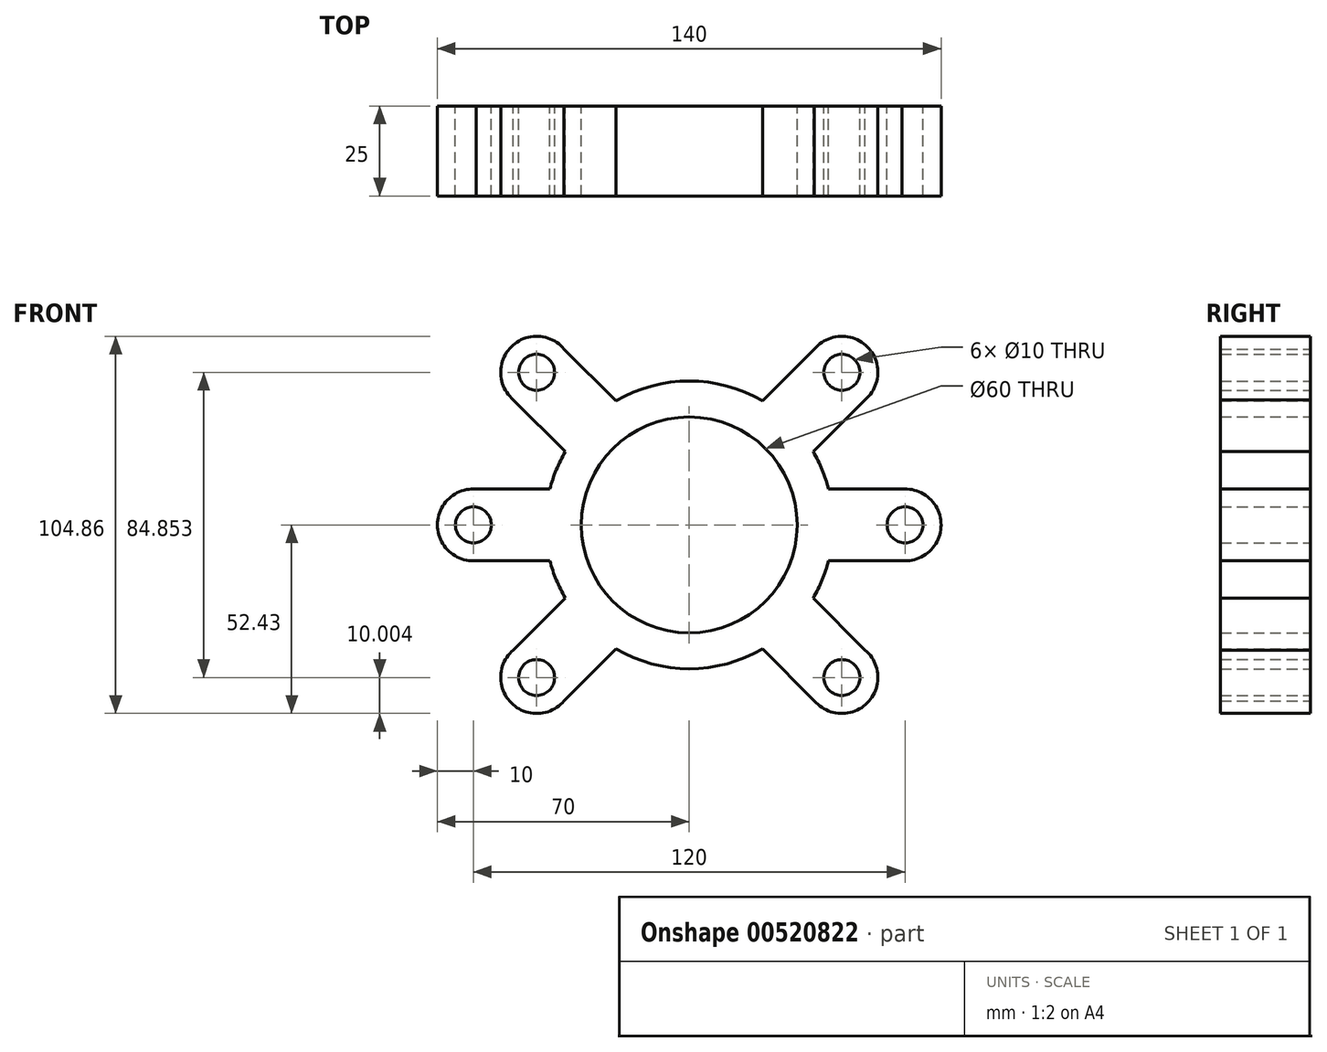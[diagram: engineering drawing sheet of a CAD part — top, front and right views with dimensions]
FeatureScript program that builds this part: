
annotation { "Feature Type Name" : "Feature", "Feature Type Description" : "" }
export const myFeature = defineFeature(function(context is Context, id is Id, definition is map)
    precondition{}
    {
        {
            var Q0;
            Q0=qCreatedBy(makeId("Front.planeOp"),FACE);
            var sketch = newSketch(context, id + "F0", { "sketchPlane" : qUnion([Q0])});
            skCircle(sketch, "E0", {"center": v(0, 0) * mm, "radius": 60 * mm, "construction": true});
            skCircle(sketch, "E1", {"center": v(0, 0) * mm, "radius": 30 * mm});
            skArc(sketch, "E2", {"start": v(38.74, 9.97) * mm, "mid": v(36.96, 15.3) * mm, "end": v(34.44, 20.35) * mm});
            skArc(sketch, "E3", {"start": v(59.17, -9.97) * mm, "mid": v(70, 0) * mm, "end": v(59.17, 9.97) * mm});
            skCircle(sketch, "E4", {"center": v(60, 0) * mm, "radius": 5 * mm});
            skLineSegment(sketch, "E5", {"start": v(59.17, 9.97) * mm, "end": v(38.74, 9.97) * mm});
            skLineSegment(sketch, "E6", {"start": v(59.17, -9.97) * mm, "end": v(38.74, -9.97) * mm});
            skLineSegment(sketch, "E7.1.0", {"start": v(34.8, 48.88) * mm, "end": v(20.35, 34.44) * mm});
            skArc(sketch, "E7.1.1", {"start": v(48.88, 34.8) * mm, "mid": v(49.5, 49.5) * mm, "end": v(34.8, 48.88) * mm});
            skLineSegment(sketch, "E7.1.2", {"start": v(48.88, 34.8) * mm, "end": v(34.44, 20.35) * mm});
            skCircle(sketch, "E7.1.3", {"center": v(42.43, 42.43) * mm, "radius": 5 * mm});
            skLineSegment(sketch, "E7.3.0", {"start": v(-48.88, 34.8) * mm, "end": v(-34.44, 20.35) * mm});
            skArc(sketch, "E7.3.1", {"start": v(-34.8, 48.88) * mm, "mid": v(-49.5, 49.5) * mm, "end": v(-48.88, 34.8) * mm});
            skLineSegment(sketch, "E7.3.2", {"start": v(-34.8, 48.88) * mm, "end": v(-20.35, 34.44) * mm});
            skCircle(sketch, "E7.3.3", {"center": v(-42.43, 42.43) * mm, "radius": 5 * mm});
            skLineSegment(sketch, "E7.4.0", {"start": v(-59.17, -9.97) * mm, "end": v(-38.74, -9.97) * mm});
            skArc(sketch, "E7.4.1", {"start": v(-59.17, 9.97) * mm, "mid": v(-70, 0) * mm, "end": v(-59.17, -9.97) * mm});
            skLineSegment(sketch, "E7.4.2", {"start": v(-59.17, 9.97) * mm, "end": v(-38.74, 9.97) * mm});
            skCircle(sketch, "E7.4.3", {"center": v(-60, 0) * mm, "radius": 5 * mm});
            skLineSegment(sketch, "E7.5.0", {"start": v(-34.8, -48.88) * mm, "end": v(-20.35, -34.44) * mm});
            skArc(sketch, "E7.5.1", {"start": v(-48.88, -34.8) * mm, "mid": v(-49.5, -49.5) * mm, "end": v(-34.8, -48.88) * mm});
            skLineSegment(sketch, "E7.5.2", {"start": v(-48.88, -34.8) * mm, "end": v(-34.44, -20.35) * mm});
            skCircle(sketch, "E7.5.3", {"center": v(-42.43, -42.43) * mm, "radius": 5 * mm});
            skLineSegment(sketch, "E7.7.0", {"start": v(48.88, -34.8) * mm, "end": v(34.44, -20.35) * mm});
            skArc(sketch, "E7.7.1", {"start": v(34.8, -48.88) * mm, "mid": v(49.5, -49.5) * mm, "end": v(48.88, -34.8) * mm});
            skLineSegment(sketch, "E7.7.2", {"start": v(34.8, -48.88) * mm, "end": v(20.35, -34.44) * mm});
            skCircle(sketch, "E7.7.3", {"center": v(42.43, -42.43) * mm, "radius": 5 * mm});
            skArc(sketch, "E8.trimOffspring", {"start": v(34.44, -20.35) * mm, "mid": v(36.96, -15.3) * mm, "end": v(38.74, -9.97) * mm});
            skArc(sketch, "E9.trimOffspring", {"start": v(-20.35, -34.44) * mm, "mid": v(0, -40) * mm, "end": v(20.35, -34.44) * mm});
            skArc(sketch, "E10.trimOffspring", {"start": v(-38.74, -9.97) * mm, "mid": v(-36.96, -15.3) * mm, "end": v(-34.44, -20.35) * mm});
            skArc(sketch, "E11.trimOffspring", {"start": v(-34.44, 20.35) * mm, "mid": v(-36.96, 15.3) * mm, "end": v(-38.74, 9.97) * mm});
            skArc(sketch, "E12.trimOffspring", {"start": v(20.35, 34.44) * mm, "mid": v(0, 40) * mm, "end": v(-20.35, 34.44) * mm});
            skLineSegment(sketch, "E13", {"start": v(0, 0) * mm, "end": v(42.43, 42.43) * mm, "construction": true});
            skLineSegment(sketch, "E14", {"start": v(0, 0) * mm, "end": v(60, 0) * mm, "construction": true});
            skSolve(sketch);
        }
        {
            var Q0;
            Q0=makeQuery(id+"F0.imprint","IMPRINT",FACE,{"disambiguationData":[TD([[makeQuery(id+"F0.imprint","IMPRINT",EDGE,{"derivedFrom":sQuery(id+"F0.wireOp",EDGE,"E1")}),-1.0]])]});
            extrude(context, id + "F1", {"entities" : qUnion([Q0]), "depth" : 25 * mm, "offsetDistance" : 25 * mm});
        }
    });
